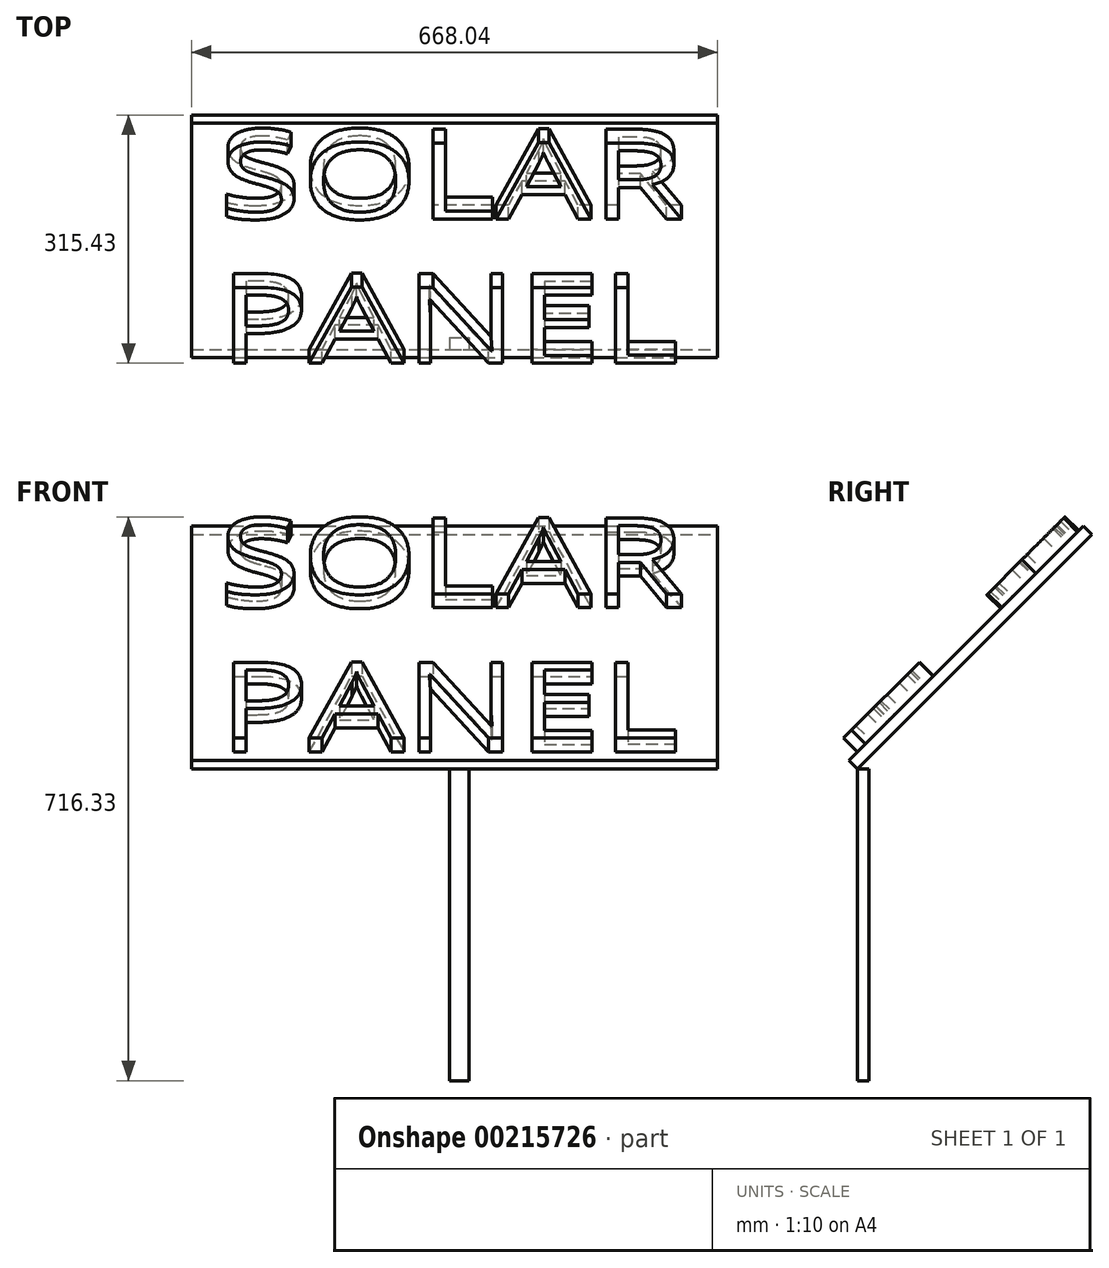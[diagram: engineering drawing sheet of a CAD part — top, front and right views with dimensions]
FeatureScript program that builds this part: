
annotation { "Feature Type Name" : "Feature", "Feature Type Description" : "" }
export const myFeature = defineFeature(function(context is Context, id is Id, definition is map)
    precondition{}
    {
        {
            var Q0;
            Q0=qCreatedBy(makeId("Front.planeOp"),FACE);
            var sketch = newSketch(context, id + "F0", { "sketchPlane" : qUnion([Q0])});
            skLineSegment(sketch, "E0.bottom", {"start": v(0, 0) * mm, "end": v(25, 0) * mm});
            skLineSegment(sketch, "E0.top", {"start": v(0, 396.13) * mm, "end": v(25, 396.13) * mm});
            skLineSegment(sketch, "E0.left", {"start": v(0, 0) * mm, "end": v(0, 396.13) * mm});
            skLineSegment(sketch, "E0.right", {"start": v(25, 0) * mm, "end": v(25, 396.13) * mm});
            skSolve(sketch);
        }
        {
            var Q0;
            Q0 = qSketchRegion(id + "F0", true);
            extrude(context, id + "F1", {"entities" : qUnion([Q0]), "oppositeDirection" : true, "depth" : 15 * mm});
        }
        {
            var Q0;
            Q0=makeQuery(id+"F1.opExtrude","SWEPT_FACE",FACE,{"disambiguationData":[OSD([sQuery(id+"F0.wireOp",EDGE,"E0.top")])]});
            var sketch = newSketch(context, id + "F2", { "sketchPlane" : qUnion([Q0])});
            skLineSegment(sketch, "E1.bottom", {"start": v(-327.59, 421.17) * mm, "end": v(340.45, 421.17) * mm});
            skLineSegment(sketch, "E1.top", {"start": v(-327.59, 0) * mm, "end": v(340.45, 0) * mm});
            skLineSegment(sketch, "E1.left", {"start": v(-327.59, 421.17) * mm, "end": v(-327.59, 0) * mm});
            skLineSegment(sketch, "E1.right", {"start": v(340.45, 421.17) * mm, "end": v(340.45, 0) * mm});
            skSolve(sketch);
        }
        {
            var Q0;
            Q0 = qSketchRegion(id + "F2", true);
            extrude(context, id + "F3", {"entities" : qUnion([Q0]), "depth" : 15 * mm});
        }
        {
            var Q0;
            Q0=makeQuery(id+"F3.opExtrude","CAP_FACE",FACE,{"disambiguationData":[OSD([sQuery(id+"F2.wireOp",EDGE,"E1.bottom"),sQuery(id+"F2.wireOp",EDGE,"E1.top"),sQuery(id+"F2.wireOp",EDGE,"E1.left"),sQuery(id+"F2.wireOp",EDGE,"E1.right")])],"isStart":false});
            var sketch = newSketch(context, id + "F4", { "sketchPlane" : qUnion([Q0])});
            skText(sketch, "E2", { "text": "SOLAR\nPANEL", "fontName": "OpenSans-Regular.ttf"});
            const initialGuessF4  = {"E2": [-0.29311, 0.2745, 1, 0, 0.13734]};
            skSetInitialGuess(sketch, initialGuessF4);
            skSolve(sketch);
        }
        {
            var Q0;
            Q0 = qSketchRegion(id + "F4", true);
            extrude(context, id + "F5", {"entities" : qUnion([Q0]), "operationType" : NewBodyOperationType.ADD, "depth" : 25 * mm});
        }
        {
            var Q0;
            Q0=makeQuery(id+"F3.opExtrude","SWEPT_BODY",BODY,{"disambiguationData":[OSD([sQuery(id+"F2.wireOp",EDGE,"E1.bottom"),sQuery(id+"F2.wireOp",EDGE,"E1.top"),sQuery(id+"F2.wireOp",EDGE,"E1.left"),sQuery(id+"F2.wireOp",EDGE,"E1.right")])]});
            var Q1;
            Q1=makeQuery(id+"F3.opExtrude","CAP_EDGE",EDGE,{"disambiguationData":[OSD([sQuery(id+"F2.wireOp",EDGE,"E1.top")])],"isStart":true});
            transform(context, id + "F6", {"entities" : qUnion([Q0]), "transformType" : TransformType.ROTATION, "transformAxis" : qUnion([Q1]), "angle" : 45 * degree, "makeCopy" : false});
        }
    });
